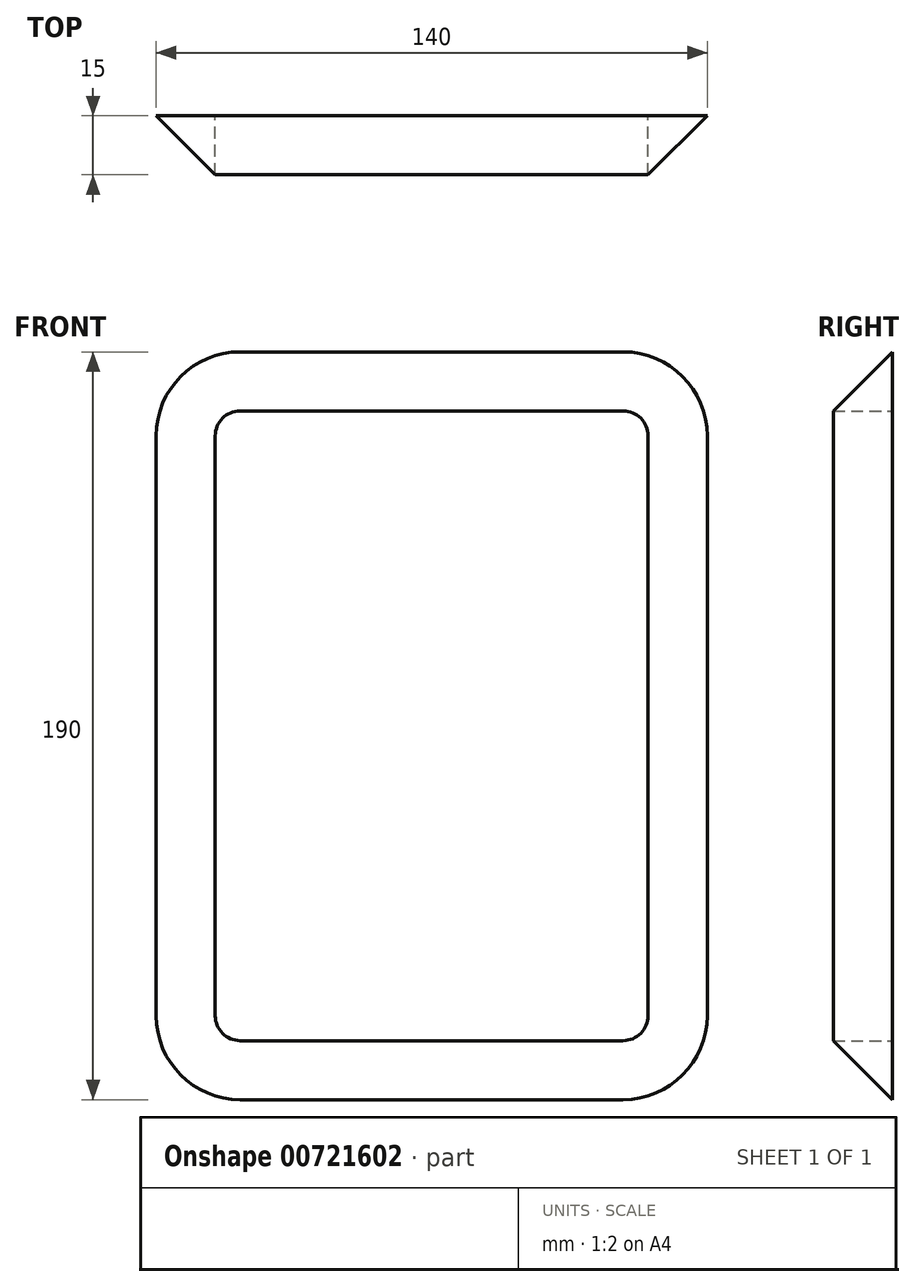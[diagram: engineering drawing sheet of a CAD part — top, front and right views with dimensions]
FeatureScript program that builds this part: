
annotation { "Feature Type Name" : "Feature", "Feature Type Description" : "" }
export const myFeature = defineFeature(function(context is Context, id is Id, definition is map)
    precondition{}
    {
        {
            var Q0;
            Q0=qCreatedBy(makeId("Front.planeOp"),FACE);
            var sketch = newSketch(context, id + "F0", { "sketchPlane" : qUnion([Q0])});
            skLineSegment(sketch, "E0.bottom", {"start": v(-6.35, 0) * mm, "end": v(-103.65, 0) * mm});
            skLineSegment(sketch, "E0.top", {"start": v(-6.35, 160) * mm, "end": v(-103.65, 160) * mm});
            skLineSegment(sketch, "E0.left", {"start": v(0, 6.35) * mm, "end": v(0, 153.65) * mm});
            skLineSegment(sketch, "E0.right", {"start": v(-110, 6.35) * mm, "end": v(-110, 153.65) * mm});
            skPoint(sketch, "E1.visualSharp", {"position": v(-110, 160) * mm});
            skArc(sketch, "E1.filletArc", {"start": v(-103.65, 160) * mm, "mid": v(-108.14, 158.14) * mm, "end": v(-110, 153.65) * mm});
            skPoint(sketch, "E2.visualSharp", {"position": v(0, 160) * mm});
            skArc(sketch, "E2.filletArc", {"start": v(0, 153.65) * mm, "mid": v(-1.86, 158.14) * mm, "end": v(-6.35, 160) * mm});
            skPoint(sketch, "E3.visualSharp", {"position": v(0, 0) * mm});
            skArc(sketch, "E3.filletArc", {"start": v(-6.35, 0) * mm, "mid": v(-1.86, 1.86) * mm, "end": v(0, 6.35) * mm});
            skPoint(sketch, "E4.visualSharp", {"position": v(-110, 0) * mm});
            skArc(sketch, "E4.filletArc", {"start": v(-110, 6.35) * mm, "mid": v(-108.14, 1.86) * mm, "end": v(-103.65, 0) * mm});
            skArc(sketch, "E5.0", {"start": v(-125, 6.35) * mm, "mid": v(-118.75, -8.75) * mm, "end": v(-103.65, -15) * mm});
            skLineSegment(sketch, "E5.1", {"start": v(-6.35, -15) * mm, "end": v(-103.65, -15) * mm});
            skLineSegment(sketch, "E5.2", {"start": v(-125, 6.35) * mm, "end": v(-125, 153.65) * mm});
            skArc(sketch, "E5.3", {"start": v(-6.35, -15) * mm, "mid": v(8.75, -8.75) * mm, "end": v(15, 6.35) * mm});
            skArc(sketch, "E5.4", {"start": v(-103.65, 175) * mm, "mid": v(-118.75, 168.75) * mm, "end": v(-125, 153.65) * mm});
            skLineSegment(sketch, "E5.5", {"start": v(-6.35, 175) * mm, "end": v(-103.65, 175) * mm});
            skArc(sketch, "E5.6", {"start": v(15, 153.65) * mm, "mid": v(8.75, 168.75) * mm, "end": v(-6.35, 175) * mm});
            skLineSegment(sketch, "E5.7", {"start": v(15, 6.35) * mm, "end": v(15, 153.65) * mm});
            skPoint(sketch, "E6.visualSharp", {"position": v(-300.79, 96.9) * mm});
            skArc(sketch, "E6.filletArc", {"start": v(-294.44, 96.9) * mm, "mid": v(-298.93, 95.04) * mm, "end": v(-300.79, 90.55) * mm});
            skPoint(sketch, "E7.visualSharp", {"position": v(-190.79, 96.9) * mm});
            skArc(sketch, "E7.filletArc", {"start": v(-190.79, 90.55) * mm, "mid": v(-192.65, 95.04) * mm, "end": v(-197.14, 96.9) * mm});
            skPoint(sketch, "E8.visualSharp", {"position": v(-190.79, -63.1) * mm});
            skArc(sketch, "E8.filletArc", {"start": v(-197.14, -63.1) * mm, "mid": v(-192.65, -61.24) * mm, "end": v(-190.79, -56.75) * mm});
            skPoint(sketch, "E9.visualSharp", {"position": v(-300.79, -63.1) * mm});
            skArc(sketch, "E9.filletArc", {"start": v(-300.79, -56.75) * mm, "mid": v(-298.93, -61.24) * mm, "end": v(-294.44, -63.1) * mm});
            skSolve(sketch);
        }
        {
            var Q0;
            Q0=makeQuery(id+"F0.imprint","IMPRINT",FACE,{"disambiguationData":[TD([[makeQuery(id+"F0.imprint","IMPRINT",EDGE,{"derivedFrom":sQuery(id+"F0.wireOp",EDGE,"E0.bottom")}),1.0]])]});
            extrude(context, id + "F1", {"entities" : qUnion([Q0]), "depth" : 15 * mm, "offsetDistance" : 25.4 * mm});
        }
        {
            var Q0;
            Q0=makeQuery(id+"F1.opExtrude","CAP_EDGE",EDGE,{"disambiguationData":[OSD([sQuery(id+"F0.wireOp",EDGE,"E5.1")])],"isStart":false});
            chamfer(context, id + "F2", {"entities" : qUnion([Q0]), "width" : 15 * mm, "tangentPropagation" : true});
        }
    });
